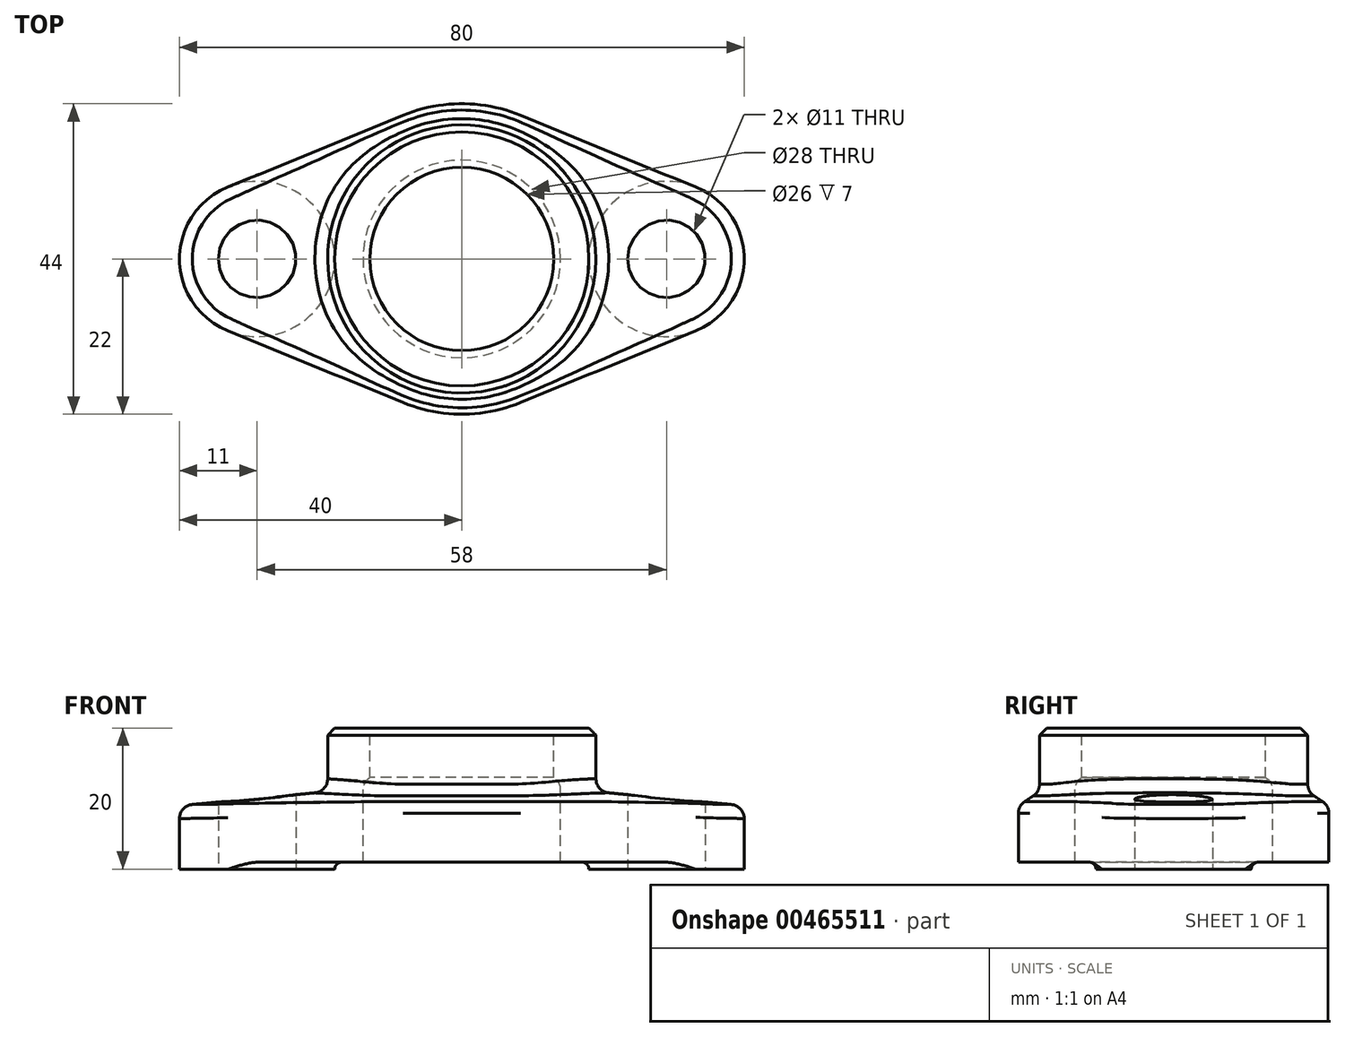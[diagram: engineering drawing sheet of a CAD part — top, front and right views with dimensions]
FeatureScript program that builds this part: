
annotation { "Feature Type Name" : "Feature", "Feature Type Description" : "" }
export const myFeature = defineFeature(function(context is Context, id is Id, definition is map)
    precondition{}
    {
        {
            var Q0;
            Q0=qCreatedBy(makeId("Top.planeOp"),FACE);
            var sketch = newSketch(context, id + "F0", { "sketchPlane" : qUnion([Q0])});
            skCircle(sketch, "E0", {"center": v(0, 0) * mm, "radius": 22 * mm});
            skLineSegment(sketch, "E1", {"start": v(0, 0) * mm, "end": v(0, 16.92) * mm, "construction": true});
            skLineSegment(sketch, "E2", {"start": v(0, 0) * mm, "end": v(29, 0) * mm, "construction": true});
            skCircle(sketch, "E3", {"center": v(29, 0) * mm, "radius": 11 * mm});
            skLineSegment(sketch, "E4", {"start": v(33.17, 10.18) * mm, "end": v(8.34, 20.36) * mm});
            skLineSegment(sketch, "E5.MirrorCS", {"start": v(33.17, -10.18) * mm, "end": v(8.34, -20.36) * mm});
            skLineSegment(sketch, "E6.MirrorCS", {"start": v(-33.17, 10.18) * mm, "end": v(-8.34, 20.36) * mm});
            skCircle(sketch, "E7.MirrorC", {"center": v(-29, 0) * mm, "radius": 11 * mm});
            skLineSegment(sketch, "E8.MirrorCS", {"start": v(-33.17, -10.18) * mm, "end": v(-8.34, -20.36) * mm});
            skSolve(sketch);
        }
        {
            var Q0;
            Q0=qSketchRegion(id+"F0",true);
            var Q1;
            {var subQ0=sQuery(id+"F0.wireOp",EDGE,"E3");var subQ1=sQuery(id+"F0.wireOp",EDGE,"E0");var subQ2=makeQuery(id+"F0.imprint","INTERSECT",VERTEX,{"disambiguationData":[OD(0.0)],"derivedFrom":[subQ1,subQ0]});Q1=makeQuery(id+"F0.imprint","IMPRINT",FACE,{"disambiguationData":[TD([[makeQuery(id+"F0.imprint","IMPRINT",EDGE,{"disambiguationData":[TD([[subQ2,1.0]])],"derivedFrom":subQ1}),1.0]])]});}
            var Q2;
            {var subQ0=sQuery(id+"F0.wireOp",EDGE,"E7.MirrorC");var subQ1=sQuery(id+"F0.wireOp",EDGE,"E0");var subQ2=makeQuery(id+"F0.imprint","INTERSECT",VERTEX,{"disambiguationData":[OD(0.0)],"derivedFrom":[subQ1,subQ0]});Q2=makeQuery(id+"F0.imprint","IMPRINT",FACE,{"disambiguationData":[TD([[makeQuery(id+"F0.imprint","IMPRINT",EDGE,{"disambiguationData":[TD([[subQ2,-1.0]])],"derivedFrom":subQ1}),1.0]])]});}
            extrude(context, id + "F1", {"entities" : qUnion([Q0, Q1, Q2]), "oppositeDirection" : true, "depth" : 9 * mm});
        }
        {
            var Q0;
            Q0=makeQuery(id+"F1.opExtrude","CAP_FACE",FACE,{"disambiguationData":[OSD([sQuery(id+"F0.wireOp",EDGE,"E0"),sQuery(id+"F0.wireOp",EDGE,"E3"),sQuery(id+"F0.wireOp",EDGE,"E4"),sQuery(id+"F0.wireOp",EDGE,"E5.MirrorCS"),sQuery(id+"F0.wireOp",EDGE,"E6.MirrorCS"),sQuery(id+"F0.wireOp",EDGE,"E7.MirrorC"),sQuery(id+"F0.wireOp",EDGE,"E8.MirrorCS")])],"isStart":true});
            cPlane(context, id + "F2", {"entities" : qUnion([Q0]), "cplaneType" : CPlaneType.OFFSET, "offset" : 2 * mm, "width" : 150 * mm, "height" : 150 * mm});
        }
        {
            var Q0;
            Q0=qCreatedBy(id+"F2.planeOp",FACE);
            var sketch = newSketch(context, id + "F3", { "sketchPlane" : qUnion([Q0])});
            skCircle(sketch, "E9", {"center": v(0, 0) * mm, "radius": 19 * mm});
            skSolve(sketch);
        }
        {
            var Q1;
            Q1=makeQuery(id+"F1.opExtrude","CAP_FACE",FACE,{"disambiguationData":[OSD([sQuery(id+"F0.wireOp",EDGE,"E0"),sQuery(id+"F0.wireOp",EDGE,"E3"),sQuery(id+"F0.wireOp",EDGE,"E4"),sQuery(id+"F0.wireOp",EDGE,"E5.MirrorCS"),sQuery(id+"F0.wireOp",EDGE,"E6.MirrorCS"),sQuery(id+"F0.wireOp",EDGE,"E7.MirrorC"),sQuery(id+"F0.wireOp",EDGE,"E8.MirrorCS")])],"isStart":true});
            var Q2;
            Q2=makeQuery(id+"F3.imprint","IMPRINT",FACE,{"disambiguationData":[TD([[makeQuery(id+"F3.imprint","IMPRINT",EDGE,{"derivedFrom":sQuery(id+"F3.wireOp",EDGE,"E9")}),1.0]])]});
            loft(context, id + "F4", {"operationType" : NewBodyOperationType.ADD, "sheetProfilesArray" : [{ "sheetProfileEntities" : qUnion([Q1]) }, { "sheetProfileEntities" : qUnion([Q2]) }]});
        }
        {
            var Q0;
            Q0 = qSketchRegion(id + "F3", true);
            extrude(context, id + "F5", {"entities" : qUnion([Q0]), "operationType" : NewBodyOperationType.ADD, "depth" : 9 * mm});
        }
        {
            var Q0;
            Q0=qCreatedBy(makeId("Front.planeOp"),FACE);
            var sketch = newSketch(context, id + "F6", { "sketchPlane" : qUnion([Q0])});
            skLineSegment(sketch, "E10", {"start": v(0, -11.17) * mm, "end": v(0, 15.2) * mm, "construction": true});
            skLineSegment(sketch, "E11.0", {"start": v(0, 11) * mm, "end": v(13, 11) * mm});
            skLineSegment(sketch, "E12.0", {"start": v(0, -9) * mm, "end": v(8.34, -9) * mm});
            skLineSegment(sketch, "E13.0", {"start": v(14, -9) * mm, "end": v(8.34, -9) * mm});
            skLineSegment(sketch, "E14", {"start": v(13, 11) * mm, "end": v(13, 4) * mm});
            skLineSegment(sketch, "E15", {"start": v(13, 4) * mm, "end": v(14, 4) * mm});
            skLineSegment(sketch, "E16", {"start": v(14, 4) * mm, "end": v(14, -9) * mm});
            skPoint(sketch, "E17.orphan", {"position": v(-19, 11) * mm});
            skPoint(sketch, "E18.orphan", {"position": v(-8.34, -9) * mm});
            skPoint(sketch, "E19.orphan", {"position": v(19, 11) * mm});
            skPoint(sketch, "E20.orphan", {"position": v(33.17, -9) * mm});
            skLineSegment(sketch, "E21", {"start": v(0, 11) * mm, "end": v(0, -9) * mm});
            skSolve(sketch);
        }
        {
            var Q0;
            Q0 = qSketchRegion(id + "F6", true);
            var Q1;
            Q1=sQuery(id+"F6.wireOp",EDGE,"E10");
            revolve(context, id + "F7", {"operationType" : NewBodyOperationType.REMOVE, "entities" : qUnion([Q0]), "axis" : qUnion([Q1]), "revolveType" : RevolveType.FULL, "oppositeDirection" : true});
        }
        {
            var Q0;
            Q0=makeQuery(id+"F1.opExtrude","CAP_FACE",FACE,{"disambiguationData":[OSD([sQuery(id+"F0.wireOp",EDGE,"E0"),sQuery(id+"F0.wireOp",EDGE,"E3"),sQuery(id+"F0.wireOp",EDGE,"E4"),sQuery(id+"F0.wireOp",EDGE,"E5.MirrorCS"),sQuery(id+"F0.wireOp",EDGE,"E6.MirrorCS"),sQuery(id+"F0.wireOp",EDGE,"E7.MirrorC"),sQuery(id+"F0.wireOp",EDGE,"E8.MirrorCS")])],"isStart":false});
            var sketch = newSketch(context, id + "F8", { "sketchPlane" : qUnion([Q0])});
            skCircle(sketch, "E22", {"center": v(29, 0) * mm, "radius": 11 * mm});
            skCircle(sketch, "E23", {"center": v(-29, 0) * mm, "radius": 11 * mm});
            skLineSegment(sketch, "E24.0.0", {"start": v(8.34, -20.36) * mm, "end": v(33.17, -10.18) * mm});
            skArc(sketch, "E24.0.1", {"start": v(33.17, -10.18) * mm, "mid": v(40, 0) * mm, "end": v(33.17, 10.18) * mm});
            skLineSegment(sketch, "E24.0.2", {"start": v(33.17, 10.18) * mm, "end": v(8.34, 20.36) * mm});
            skArc(sketch, "E24.0.3", {"start": v(8.34, 20.36) * mm, "mid": v(0, 22) * mm, "end": v(-8.34, 20.36) * mm});
            skLineSegment(sketch, "E24.0.4", {"start": v(-8.34, 20.36) * mm, "end": v(-33.17, 10.18) * mm});
            skArc(sketch, "E24.0.5", {"start": v(-33.17, 10.18) * mm, "mid": v(-40, 0) * mm, "end": v(-33.17, -10.18) * mm});
            skLineSegment(sketch, "E24.0.6", {"start": v(-33.17, -10.18) * mm, "end": v(-8.34, -20.36) * mm});
            skArc(sketch, "E24.0.7", {"start": v(-8.34, -20.36) * mm, "mid": v(0, -22) * mm, "end": v(8.34, -20.36) * mm});
            skCircle(sketch, "E25.0", {"center": v(0, 0) * mm, "radius": 14 * mm});
            skCircle(sketch, "E26", {"center": v(29, 0) * mm, "radius": 5.5 * mm});
            skCircle(sketch, "E27", {"center": v(-29, 0) * mm, "radius": 5.5 * mm});
            skSolve(sketch);
        }
        {
            var Q0;
            Q0=makeQuery(id+"F8.imprint","IMPRINT",FACE,{"disambiguationData":[TD([[makeQuery(id+"F8.imprint","IMPRINT",EDGE,{"disambiguationData":[OD(0.0)],"derivedFrom":sQuery(id+"F8.wireOp",EDGE,"E22")}),-1.0]])]});
            extrude(context, id + "F9", {"entities" : qUnion([Q0]), "operationType" : NewBodyOperationType.REMOVE, "oppositeDirection" : true, "depth" : 1 * mm});
        }
        {
            var Q0;
            Q0=makeQuery(id+"F8.imprint","IMPRINT",FACE,{"disambiguationData":[TD([[makeQuery(id+"F8.imprint","IMPRINT",EDGE,{"derivedFrom":sQuery(id+"F8.wireOp",EDGE,"E26")}),1.0]])]});
            var Q1;
            Q1=makeQuery(id+"F8.imprint","IMPRINT",FACE,{"disambiguationData":[TD([[makeQuery(id+"F8.imprint","IMPRINT",EDGE,{"derivedFrom":sQuery(id+"F8.wireOp",EDGE,"E27")}),1.0]])]});
            extrude(context, id + "F10", {"entities" : qUnion([Q0, Q1]), "operationType" : NewBodyOperationType.REMOVE, "endBound" : BoundingType.THROUGH_ALL, "oppositeDirection" : true, "depth" : 25 * mm});
        }
        {
            var Q0;
            Q0=makeQuery(id+"F10.boolean.opBoolean","COPY",EDGE,{"derivedFrom":makeQuery(id+"F10.opExtrude","CAP_EDGE",EDGE,{"disambiguationData":[OSD([sQuery(id+"F8.wireOp",EDGE,"E26")])],"isStart":true})});
            var Q1;
            Q1=makeQuery(id+"F10.boolean.opBoolean","COPY",EDGE,{"derivedFrom":makeQuery(id+"F10.opExtrude","CAP_EDGE",EDGE,{"disambiguationData":[OSD([sQuery(id+"F8.wireOp",EDGE,"E27")])],"isStart":true})});
            var Q2;
            Q2=makeQuery(id+"F7.boolean.opBoolean","COPY",EDGE,{"derivedFrom":makeQuery(id+"F7.opRevolve","SWEPT_EDGE",EDGE,{"disambiguationData":[OSD([sQuery(id+"F6.wireOp",EDGE,"E11.0"),sQuery(id+"F6.wireOp",EDGE,"E14")])]})});
            var Q3;
            Q3=makeQuery(id+"F5.opExtrude","CAP_EDGE",EDGE,{"disambiguationData":[OSD([sQuery(id+"F3.wireOp",EDGE,"E9")])],"isStart":false});
            chamfer(context, id + "F11", {"entities" : qUnion([Q0, Q1, Q2, Q3]), "width" : 1 * mm, "tangentPropagation" : true});
        }
        {
            var Q0;
            {var subQ0=sQuery(id+"F3.wireOp",EDGE,"E9");Q0=makeQuery(id+"F5.boolean.opBoolean","MERGE",EDGE,{"derivedFrom":[makeQuery(id+"F4.opLoft","MID_CAP_EDGE",EDGE,{"disambiguationData":[OSD([sQuery(id+"F0.wireOp",EDGE,"E0"),sQuery(id+"F0.wireOp",EDGE,"E3"),sQuery(id+"F0.wireOp",EDGE,"E4"),sQuery(id+"F0.wireOp",EDGE,"E5.MirrorCS"),subQ0])],"capPos":1.0}),makeQuery(id+"F5.opExtrude","CAP_EDGE",EDGE,{"disambiguationData":[OSD([subQ0])],"isStart":true})]});}
            var Q1;
            {var subQ0=sQuery(id+"F0.wireOp",EDGE,"E3");Q1=makeQuery(id+"F4.boolean.opBoolean","MERGE",EDGE,{"derivedFrom":[makeQuery(id+"F1.opExtrude","CAP_EDGE",EDGE,{"disambiguationData":[OSD([subQ0])],"isStart":true}),makeQuery(id+"F4.opLoft","MID_CAP_EDGE",EDGE,{"disambiguationData":[OSD([subQ0,sQuery(id+"F0.wireOp",EDGE,"E4"),sQuery(id+"F0.wireOp",EDGE,"E5.MirrorCS")])],"capPos":0.0})]});}
            var Q2;
            Q2=makeQuery(id+"F7.boolean.opBoolean","COPY",EDGE,{"derivedFrom":makeQuery(id+"F7.opRevolve","SWEPT_EDGE",EDGE,{"disambiguationData":[OSD([sQuery(id+"F6.wireOp",EDGE,"E15"),sQuery(id+"F6.wireOp",EDGE,"E16")])]})});
            fillet(context, id + "F12", {"entities" : qUnion([Q0, Q1, Q2]), "radius" : 2 * mm, "tangentPropagation" : true, "allowEdgeOverflow" : false});
        }
        {
            var Q0;
            Q0=makeQuery(id+"F9.boolean.opBoolean","COPY",EDGE,{"derivedFrom":makeQuery(id+"F9.opExtrude","CAP_EDGE",EDGE,{"disambiguationData":[OSD([sQuery(id+"F8.wireOp",EDGE,"E23")])],"isStart":false})});
            var Q1;
            Q1=makeQuery(id+"F9.boolean.opBoolean","COPY",EDGE,{"derivedFrom":makeQuery(id+"F9.opExtrude","CAP_EDGE",EDGE,{"disambiguationData":[OSD([sQuery(id+"F8.wireOp",EDGE,"E22")])],"isStart":false})});
            fillet(context, id + "F13", {"entities" : qUnion([Q0, Q1]), "radius" : 1 * mm, "tangentPropagation" : true, "allowEdgeOverflow" : false});
        }
    });
